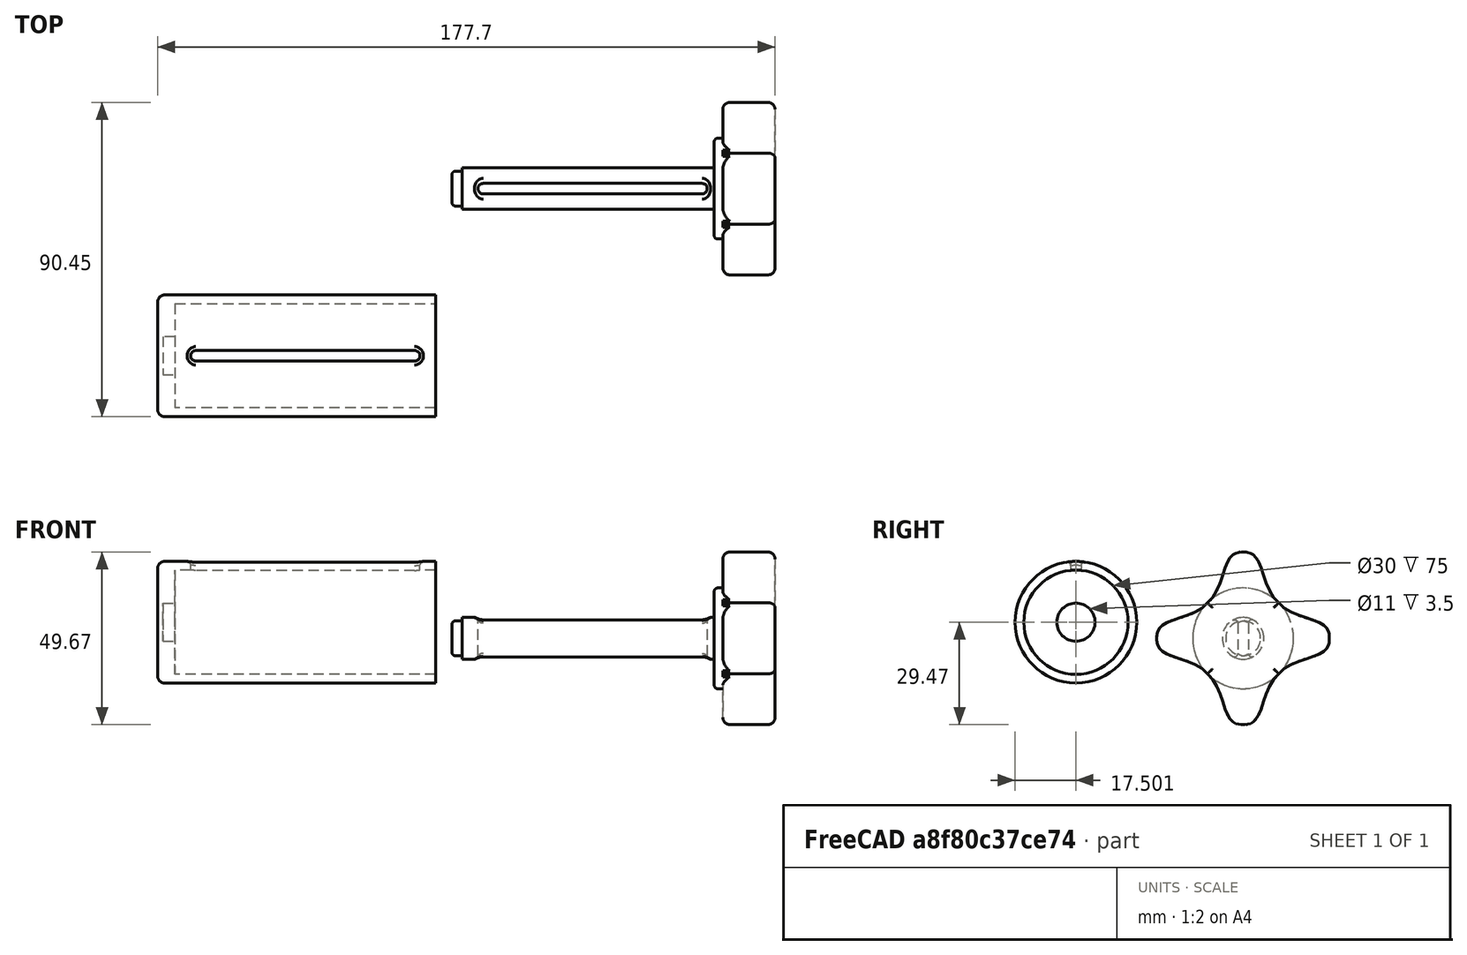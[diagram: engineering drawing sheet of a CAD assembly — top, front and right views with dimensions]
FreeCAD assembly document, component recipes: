
FREECAD ASSEMBLY — COMPONENT RECIPES ("tomato_paste_squeezer")

This assembly document has 2 components, labeled P0..P1 below (a component is one placed body or linked part). 2 of them carry a construction recipe — the FreeCAD feature program that regenerates the part from scratch, quoted from this document or its linked companion documents; the rest are supplied as boundary geometry only. No exploded tour is included for this assembly.
COMPONENT P0 — recipe-attached ("avvitatore001", modeled in this document).
Construction recipe (the document's own serialized feature program — sketch geometry with constraints, then the solid features built on it; lengths are millimeters unless a unit is written):

FEATURE [Sketcher::SketchObject] Sketch003
  ArcFitTolerance = 1e-06
  AttachmentSupport = -> [YZ_Plane001]
  FullyConstrained = true
  MakeInternals = false
  MapMode = 5
  Placement = pos=(0,0,0) rot=(0.57735,0.57735,0.57735;2.0944rad)
  sketch-geometry (1):
    g0: Circle CenterX=0 CenterY=0 CenterZ=0 NormalX=0 NormalY=0 NormalZ=1 AngleXU=0 Radius=14.5
  constraints (2):
    c: Diameter(g0) = 29
    c: Coincident(g0,g-1)
FEATURE [PartDesign::Pad] Pad002
  Direction = (1,0,0)
  Length = 2.5
  Length2 = 10
  Placement = pos=(0,0,0) rot=(1,1,1;2.0944rad)
  Profile = -> Sketch003
  ReferenceAxis = -> Sketch003 [N_Axis]
  Refine = true
  Suppressed = false
  Type = 0
FEATURE [Sketcher::SketchObject] Sketch004
  ArcFitTolerance = 1e-06
  AttachmentSupport = -> [Pad002]
  FullyConstrained = true
  MakeInternals = false
  MapMode = 5
  Placement = pos=(2.5,-6e-16,3e-16) rot=(0.57735,0.57735,0.57735;2.0944rad)
  sketch-geometry (1):
    g0: Circle CenterX=0 CenterY=0 CenterZ=0 NormalX=0 NormalY=0 NormalZ=1 AngleXU=0 Radius=25
  constraints (2):
    c: Diameter(g0) = 50
    c: Coincident(g0,g-1)
FEATURE [PartDesign::Pad] Pad003
  BaseFeature = -> Pad002
  Direction = (1,0,0)
  Length = 15
  Length2 = 10
  Placement = pos=(0,0,0) rot=(1,1,1;2.0944rad)
  Profile = -> Sketch004
  ReferenceAxis = -> Sketch004 [N_Axis]
  Refine = true
  Suppressed = false
  Type = 0
FEATURE [Sketcher::SketchObject] Sketch005
  ArcFitTolerance = 1e-06
  AttachmentSupport = -> [Pad003]
  ExternalGeometry = -> [Pad003]
  FullyConstrained = true
  MakeInternals = false
  MapMode = 5
  Placement = pos=(17.5,-3.9e-15,1.9e-15) rot=(0.57735,0.57735,0.57735;2.0944rad)
  sketch-geometry (20):
    g0: LineSegment [constr] StartX=0 StartY=0 StartZ=0 EndX=-10.253 EndY=10.253 EndZ=0
    g1: LineSegment [constr] StartX=0 StartY=0 StartZ=0 EndX=10.253 EndY=10.253 EndZ=0
    g2: LineSegment [constr] StartX=0 StartY=0 StartZ=0 EndX=0 EndY=25 EndZ=0
    g3-g9: Circle [constr] x7 (B-spline internal-alignment scaffolding for g10; pole/knot coordinates omitted)
    g10: BSplineCurve PolesCount=7 KnotsCount=5 Degree=3 IsPeriodic=0
    g11-g15: GeomPoint [constr] x5 (B-spline internal-alignment scaffolding for g10; pole/knot coordinates omitted)
    g16: LineSegment StartX=-10.253 StartY=10.253 StartZ=0 EndX=-25.253 EndY=25.253 EndZ=0
    g17: LineSegment StartX=-25.253 StartY=25.253 StartZ=0 EndX=0 EndY=46.4 EndZ=0
    g18: LineSegment StartX=0 StartY=46.4 StartZ=0 EndX=25.253 EndY=25.253 EndZ=0
    g19: LineSegment StartX=10.253 StartY=10.253 StartZ=0 EndX=25.253 EndY=25.253 EndZ=0
  constraints (35):
    c: Coincident(g0,g-1)
    c: Coincident(g1,g0)
    c: Angle(g-1,g1) = 0.785398
    c: Angle(g0,g-1) = 0.785398
    c: Coincident(g2,g0)
    c: PointOnObject(g2,g-4)
    c: Vertical(g2)
    c: PointOnObject(g0,g-3)
    c: PointOnObject(g1,g-3)
    c: Weight(g3) = 1
    c: Equal(g3, g4-g9) x6
    c: InternalAlignment(g3-g9 -> g10) x7
    c: InternalAlignment(g11-g15 -> g10) x5
    c: Coincident(g3,g0)
    c: PointOnObject(g4,g-3)
    c: PointOnObject(g5,g-4)
    c: Coincident(g6,g2)
    c: PointOnObject(g7,g-4)
    c: PointOnObject(g8,g-3)
    c: Coincident(g9,g1)
    c: DistanceX(g-1,g8) = 7
    c: DistanceX(g4,g-1) = 7
    c: DistanceX(g-1,g7) = 5
    c: DistanceX(g5,g-1) = 5
    c: Coincident(g16,g10)
    c: Coincident(g17,g16)
    c: PointOnObject(g17,g-2)
    c: Coincident(g18,g17)
    c: Coincident(g19,g10)
    c: Coincident(g19,g18)
    c: Angle(g19,g1) = 3.14159
    c: Angle(g0,g16) = 3.14159
    c: DistanceY(g19,g19) = 15
    c: DistanceY(g16,g16) = 15
    c: DistanceY(g-1,g17) = 46.4
FEATURE [PartDesign::Pocket] Pocket001
  BaseFeature = -> Pad003
  Direction = (-1,0,0)
  Length = 0
  Length2 = 5
  Placement = pos=(0,0,0) rot=(1,1,1;2.0944rad)
  Profile = -> Sketch005
  ReferenceAxis = -> Sketch005 [N_Axis]
  Refine = true
  Suppressed = false
  Type = 3
  UpToFace = -> Pad003 [Face3]
FEATURE [PartDesign::PolarPattern] PolarPattern
  Angle = 360
  Axis = -> Sketch005 [N_Axis]
  BaseFeature = -> Pocket001
  Mode = 0
  Occurrences = 4
  Offset = 120
  Originals = -> [Pocket001]
  Placement = pos=(0,0,0) rot=(1,1,1;2.0944rad)
  Refine = true
  Suppressed = false
  TransformMode = 0
FEATURE [Sketcher::SketchObject] Sketch006
  ArcFitTolerance = 1e-06
  AttachmentSupport = -> [PolarPattern]
  FullyConstrained = true
  MakeInternals = false
  MapMode = 5
  Placement = pos=(0,0,0) rot=(0.57735,0.57735,-0.57735;4.18879rad)
  sketch-geometry (1):
    g0: Circle CenterX=0 CenterY=0 CenterZ=0 NormalX=0 NormalY=0 NormalZ=1 AngleXU=0 Radius=6
  constraints (2):
    c: Diameter(g0) = 12
    c: Coincident(g0,g-1)
FEATURE [PartDesign::Pad] Pad004
  BaseFeature = -> PolarPattern
  Direction = (-1,0,0)
  Length = 72.5
  Length2 = 10
  Placement = pos=(0,0,0) rot=(1,1,1;2.0944rad)
  Profile = -> Sketch006 [Edge1]
  ReferenceAxis = -> Sketch006 [N_Axis]
  Refine = true
  Suppressed = false
  Type = 0
FEATURE [Sketcher::SketchObject] Sketch007
  ArcFitTolerance = 1e-06
  AttachmentSupport = -> [XY_Plane001]
  ExternalGeometry = -> [Pad004]
  FullyConstrained = true
  MakeInternals = false
  MapMode = 5
  sketch-geometry (4):
    g0: ArcOfCircle CenterX=-66.5 CenterY=1e-16 CenterZ=0 NormalX=0 NormalY=0 NormalZ=1 AngleXU=0 Radius=1.5 StartAngle=1.5708 EndAngle=4.71239
    g1: ArcOfCircle CenterX=-3.5 CenterY=0 CenterZ=0 NormalX=0 NormalY=0 NormalZ=1 AngleXU=0 Radius=1.5 StartAngle=4.71239 EndAngle=7.85398
    g2: LineSegment StartX=-66.5 StartY=1.5 StartZ=0 EndX=-3.5 EndY=1.5 EndZ=0
    g3: LineSegment StartX=-66.5 StartY=-1.5 StartZ=0 EndX=-3.5 EndY=-1.5 EndZ=0
  constraints (10):
    c: Tangent(g0,g2) = 1.5708
    c: Tangent(g0,g3) = -1.5708
    c: Tangent(g1,g2) = 1.5708
    c: Tangent(g1,g3) = -1.5708
    c: Equal(g0,g1)
    c: Radius(g0) = 1.5
    c: Horizontal(g2)
    c: PointOnObject(g1,g-1)
    c: DistanceX(g2,g2) = 63
    c: Distance(g1,g-3) = 6
FEATURE [PartDesign::Pocket] Pocket002
  BaseFeature = -> Pad004
  Direction = (0,0,-1)
  Length = 5
  Length2 = 5
  Midplane = true
  Placement = pos=(0,0,0) rot=(1,1,1;2.0944rad)
  Profile = -> Sketch007
  ReferenceAxis = -> Sketch007 [N_Axis]
  Refine = true
  Suppressed = false
  Type = 1
FEATURE [Sketcher::SketchObject] Sketch008
  ArcFitTolerance = 1e-06
  AttachmentSupport = -> [Pocket002]
  FullyConstrained = true
  MakeInternals = false
  MapMode = 5
  Placement = pos=(-72.5,3.22e-14,-1.61e-14) rot=(0.57735,0.57735,-0.57735;4.18879rad)
  sketch-geometry (1):
    g0: Circle CenterX=0 CenterY=0 CenterZ=0 NormalX=0 NormalY=0 NormalZ=1 AngleXU=0 Radius=5
  constraints (2):
    c: Diameter(g0) = 10
    c: Coincident(g0,g-1)
FEATURE [PartDesign::Pad] Pad005
  BaseFeature = -> Pocket002
  Direction = (-1,0,0)
  Length = 3
  Length2 = 10
  Placement = pos=(0,0,0) rot=(1,1,1;2.0944rad)
  Profile = -> Sketch008
  ReferenceAxis = -> Sketch008 [N_Axis]
  Refine = true
  Suppressed = false
  Type = 0
FEATURE [PartDesign::Fillet] Fillet
  Base = -> Pad005 [Edge55,Edge15,Edge43,Edge44]
  BaseFeature = -> Pad005
  Placement = pos=(0,0,0) rot=(1,1,1;2.0944rad)
  Radius = 1
  Refine = true
  SupportTransform = false
  Suppressed = false
  UseAllEdges = false
FEATURE [PartDesign::Fillet] Fillet001
  Base = -> Fillet [Edge25,Edge18,Edge22,Edge34,Edge31,Edge36,Edge28,Edge38]
  BaseFeature = -> Fillet
  Placement = pos=(0,0,0) rot=(1,1,1;2.0944rad)
  Radius = 2
  Refine = true
  SupportTransform = false
  Suppressed = false
  UseAllEdges = false
FEATURE [PartDesign::Body] Body001  label="avvitatore"
  AllowCompound = false
  Group = -> [Sketch003,Pad002,Sketch004,Pad003,Sketch005,Pocket001,PolarPattern,Sketch006,Pad004,Sketch007,Pocket002,Sketch008,Pad005,Fillet,Fillet001]
  Origin = -> Origin001
  Placement = pos=(167.73,280.208,-4.63576) rot=(0,0,1;0rad)
  Tip = -> Fillet001
COMPONENT P1 — recipe-attached ("corpo_principale001", modeled in this document).
Construction recipe (the document's own serialized feature program — sketch geometry with constraints, then the solid features built on it; lengths are millimeters unless a unit is written):

FEATURE [Sketcher::SketchObject] Sketch
  ArcFitTolerance = 1e-06
  AttachmentSupport = -> [YZ_Plane]
  FullyConstrained = true
  MakeInternals = false
  MapMode = 5
  Placement = pos=(0,0,0) rot=(0.57735,0.57735,0.57735;2.0944rad)
  sketch-geometry (2):
    g0: Circle CenterX=0 CenterY=0 CenterZ=0 NormalX=0 NormalY=0 NormalZ=1 AngleXU=0 Radius=15
    g1: Circle CenterX=0 CenterY=0 CenterZ=0 NormalX=0 NormalY=0 NormalZ=1 AngleXU=0 Radius=17.5
  constraints (4):
    c: Diameter(g0) = 30
    c: Coincident(g0,g-1)
    c: Diameter(g1) = 35
    c: Coincident(g1,g0)
FEATURE [PartDesign::Pad] Pad
  Direction = (1,0,0)
  Length = 75
  Length2 = 10
  Placement = pos=(0,0,0) rot=(1,1,1;2.0944rad)
  Profile = -> Sketch
  ReferenceAxis = -> Sketch [N_Axis]
  Refine = true
  Suppressed = false
  Type = 0
FEATURE [PartDesign::Plane] DatumPlane
  AttachmentOffset = pos=(0,0,17.5) rot=(0,0,1;0rad)
  AttachmentSupport = -> [XY_Plane]
  Length = 114.142
  MapMode = 5
  Placement = pos=(0,0,17.5) rot=(0,0,1;0rad)
  ResizeMode = 0
  Width = 64.1421
FEATURE [Sketcher::SketchObject] Sketch001
  ArcFitTolerance = 1e-06
  AttachmentSupport = -> [DatumPlane]
  ExternalGeometry = -> [Pad]
  FullyConstrained = true
  MakeInternals = false
  MapMode = 5
  Placement = pos=(0,0,17.5) rot=(0,0,1;0rad)
  sketch-geometry (4):
    g0: ArcOfCircle CenterX=6 CenterY=0 CenterZ=0 NormalX=0 NormalY=0 NormalZ=1 AngleXU=0 Radius=1.5 StartAngle=1.5708 EndAngle=4.71239
    g1: ArcOfCircle CenterX=69 CenterY=0 CenterZ=0 NormalX=0 NormalY=0 NormalZ=1 AngleXU=0 Radius=1.5 StartAngle=4.71239 EndAngle=7.85398
    g2: LineSegment StartX=6 StartY=1.5 StartZ=0 EndX=69 EndY=1.5 EndZ=0
    g3: LineSegment StartX=6 StartY=-1.5 StartZ=0 EndX=69 EndY=-1.5 EndZ=0
  constraints (10):
    c: Tangent(g0,g2) = 1.5708
    c: Tangent(g0,g3) = -1.5708
    c: Tangent(g1,g2) = 1.5708
    c: Tangent(g1,g3) = -1.5708
    c: Equal(g0,g1)
    c: Horizontal(g3)
    c: Radius(g0) = 1.5
    c: PointOnObject(g0,g-1)
    c: DistanceX(g2,g2) = 63
    c: Distance(g0,g-1) = 6
FEATURE [PartDesign::Pocket] Pocket
  BaseFeature = -> Pad
  Direction = (0,0,-1)
  Length = 5
  Length2 = 5
  Placement = pos=(0,0,0) rot=(1,1,1;2.0944rad)
  Profile = -> Sketch001
  ReferenceAxis = -> Sketch001 [N_Axis]
  Refine = true
  Suppressed = false
  Type = 2
FEATURE [Sketcher::SketchObject] Sketch002
  ArcFitTolerance = 1e-06
  AttachmentSupport = -> [Pocket]
  FullyConstrained = true
  MakeInternals = false
  MapMode = 5
  Placement = pos=(0,0,0) rot=(0.57735,0.57735,-0.57735;4.18879rad)
  sketch-geometry (1):
    g0: Circle CenterX=0 CenterY=0 CenterZ=0 NormalX=0 NormalY=0 NormalZ=1 AngleXU=0 Radius=17.5
  constraints (2):
    c: Diameter(g0) = 35
    c: Coincident(g0,g-1)
FEATURE [PartDesign::Pad] Pad001
  BaseFeature = -> Pocket
  Direction = (-1,0,0)
  Length = 5
  Length2 = 10
  Placement = pos=(0,0,0) rot=(1,1,1;2.0944rad)
  Profile = -> Sketch002
  ReferenceAxis = -> Sketch002 [N_Axis]
  Refine = true
  Suppressed = false
  Type = 0
FEATURE [Sketcher::SketchObject] Sketch009
  ArcFitTolerance = 1e-06
  AttachmentSupport = -> [Pad001]
  FullyConstrained = true
  MakeInternals = false
  MapMode = 5
  Placement = pos=(0,0,0) rot=(0.57735,0.57735,0.57735;2.0944rad)
  sketch-geometry (1):
    g0: Circle CenterX=0 CenterY=0 CenterZ=0 NormalX=0 NormalY=0 NormalZ=1 AngleXU=0 Radius=5.5
  constraints (2):
    c: Diameter(g0) = 11
    c: Coincident(g0,g-1)
FEATURE [PartDesign::Pocket] Pocket003
  BaseFeature = -> Pad001
  Direction = (-1,0,0)
  Length = 3.5
  Length2 = 5
  Placement = pos=(0,0,0) rot=(1,1,1;2.0944rad)
  Profile = -> Sketch009
  ReferenceAxis = -> Sketch009 [N_Axis]
  Refine = true
  Suppressed = false
  Type = 0
FEATURE [PartDesign::Fillet] Fillet002
  Base = -> Pocket003 [Edge1]
  BaseFeature = -> Pocket003
  Placement = pos=(0,0,0) rot=(1,1,1;2.0944rad)
  Radius = 2
  Refine = true
  SupportTransform = false
  Suppressed = false
  UseAllEdges = false
FEATURE [PartDesign::Fillet] Fillet003
  Base = -> Fillet002 [Edge9,Edge6]
  BaseFeature = -> Fillet002
  Placement = pos=(0,0,0) rot=(1,1,1;2.0944rad)
  Radius = 1
  Refine = true
  SupportTransform = false
  Suppressed = false
  UseAllEdges = false
FEATURE [PartDesign::Body] Body  label="corpo_principale"
  AllowCompound = false
  Group = -> [Sketch,Pad,DatumPlane,Sketch001,Pocket,Sketch002,Pad001,Sketch009,Pocket003,Fillet002,Fillet003]
  Origin = -> Origin
  Placement = pos=(12.535,232.091,0) rot=(0,0,1;0rad)
  Tip = -> Fillet003
PROVENANCE & LICENSES
A FreeCAD (.FCStd) document from a public repository crawl; recipes are the document's own serialized feature recipes (and, for linked parts, companion documents' recipes).
License: as declared in the source repository (recorded in the dataset sidecar).
